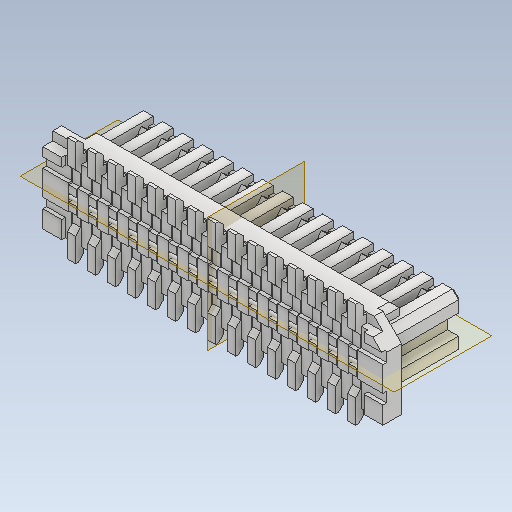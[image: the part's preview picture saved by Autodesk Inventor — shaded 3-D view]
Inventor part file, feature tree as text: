
AUTODESK INVENTOR PART (.ipt)
format: ipt  version: 2021 (Build 250183000, 183)  size: 901,120 bytes
history: native  units: mm
features: plane x2
ambient origin geometry x8: Origin, YZ Plane, XZ Plane, XY Plane, X Axis, Y Axis, Z Axis, Center Point
bodies: Solid1 (feature_tree)
feature tree (2):
  plane  "Work Plane1"
  plane  "Work Plane2"
